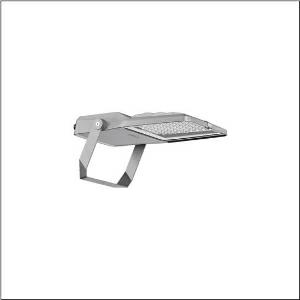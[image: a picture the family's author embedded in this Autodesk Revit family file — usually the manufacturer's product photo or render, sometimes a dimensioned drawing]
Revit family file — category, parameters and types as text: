
# Revit family: floodlight_fl_21_iq_mini___rs12_5xa7771b2b1a_fd88
name_source: partatom
category: Lighting Fixtures
units: mm (PartAtom-declared; Revit-internal decimal feet)

## family parameters
Cut with Voids When Loaded = No
Host = Face
Light Source = No
Part Type = Normal
Room Calculation Point = No
Round Connector Dimension = Use Diameter
Shared = No

## types (1)
- --- (1 x LED, 6300 lm, 45.5 W, 3000K)
    Apparent Load = 46 VA
    CIE Flux Codes = 79 92 99 100 100
    Color Rendering = 70
    Color Temperature = 3000K
    Default Elevation = 1800 mm
    Description = Floodlight FL 21 iQ mini, floodlight, primary light control with lens, of PMMA, primary optical cover: protective disc, of toughened safety glass, transparent, light distribution: RS12, light emission: direct distribution, installation type: surface-mounted, LED, High Power LED, rated luminous flux: 6.300lm, luminous efficacy: 139lm/W, light colour: 730, colour temperature: 3000K, control gear: iQ Comfort/DALI, control: Auto-Match, Temp-Guard, Lumen-Switch, Night-Set, Smart-Wire, Light-Fading, Desk-Remote (wireless, voltage-free reading and setting of iQ features in the workshop via application-optimized NFC function/RFID function), optimised constant luminous flux control (CLO 2.0), with terminal, 6-pole, mains connection: 220..240V, AC, 50/60Hz, start of lifetime: 46W, end of service life: 48W, reduction: 22W, luminaire housing, of diecast aluminium, powder-coated, Siteco® metallic grey (DB 702S), corrosivity category C5 mid according to DIN EN ISO 12944, suitable for swimming pools, chlorine-resistant, sealing non-destructively replaceable, mounting bracket, of steel, galvanised, powder-coated, Siteco® metallic grey (DB 702S), protection rating (complete): IP66, insulation class (complete): insulation class II (safety insulation), certification: CE, ENEC, VDE, protection symbol: D, impact resistance: IK08, permissible operating ambient temperature: -40..+40°C, permissible operating ambient temperature for outdoor applications: -40..+50°C, standard: DIN EN 12944, LABS conformity tested according to VDMA 24364:2018-05, packaging unit: 1 piece

Light Distribution: RS12
    Height = 70 mm
    Lamp = 1 x LED
    Lamp Light Flux = 6300 lm
    Lamp Power = 45.5 W
    Lamp count = 1
    Length = 485 mm
    Luminous efficacy = 138 lm/W
    Manufacturer = Siteco
    ModVariant = No
    Model = 5XA7771B2B1A
    Mounting Place = Wall
    Mounting Type = Surface mounted
    Number of Poles = 1
    OnlyDefault = Yes
    Power Factor = 1
    Product Name = Floodlight FL 21 iQ mini | RS12
    Product group = floodlight | wall mounted
    ProductGroupID = 2001
    Protection Class = Protection class II
    Protection Degree = IP 66
    RLX_Detail_Level = 1
    RLX_Emergency_Light_Flux = 0 lm
    RLX_Emergency_Type = 0
    RLX_Emergency_Type_DB = No
    RlxData = <blob elided: 91005 chars, md5=965879b3>
    Socket = socket
    Standby Power = 0 W
    System Light Flux = 6300 lm
    System Power = 46 W
    Type Comments = factory setting: luminous flux: 100 % | dim-lin: 254 | 463 mA
    Type Image = l_1006845.jpg
    URL = http://relux.com
    VarID = @adj_167996
    Voltage = 0 V
    Weight = 0.00 kg
    Width = 337 mm

## geometry (parser evidence)
native form markers: Blend x4, Sweep x13
no freeform markers — native parametric forms only
